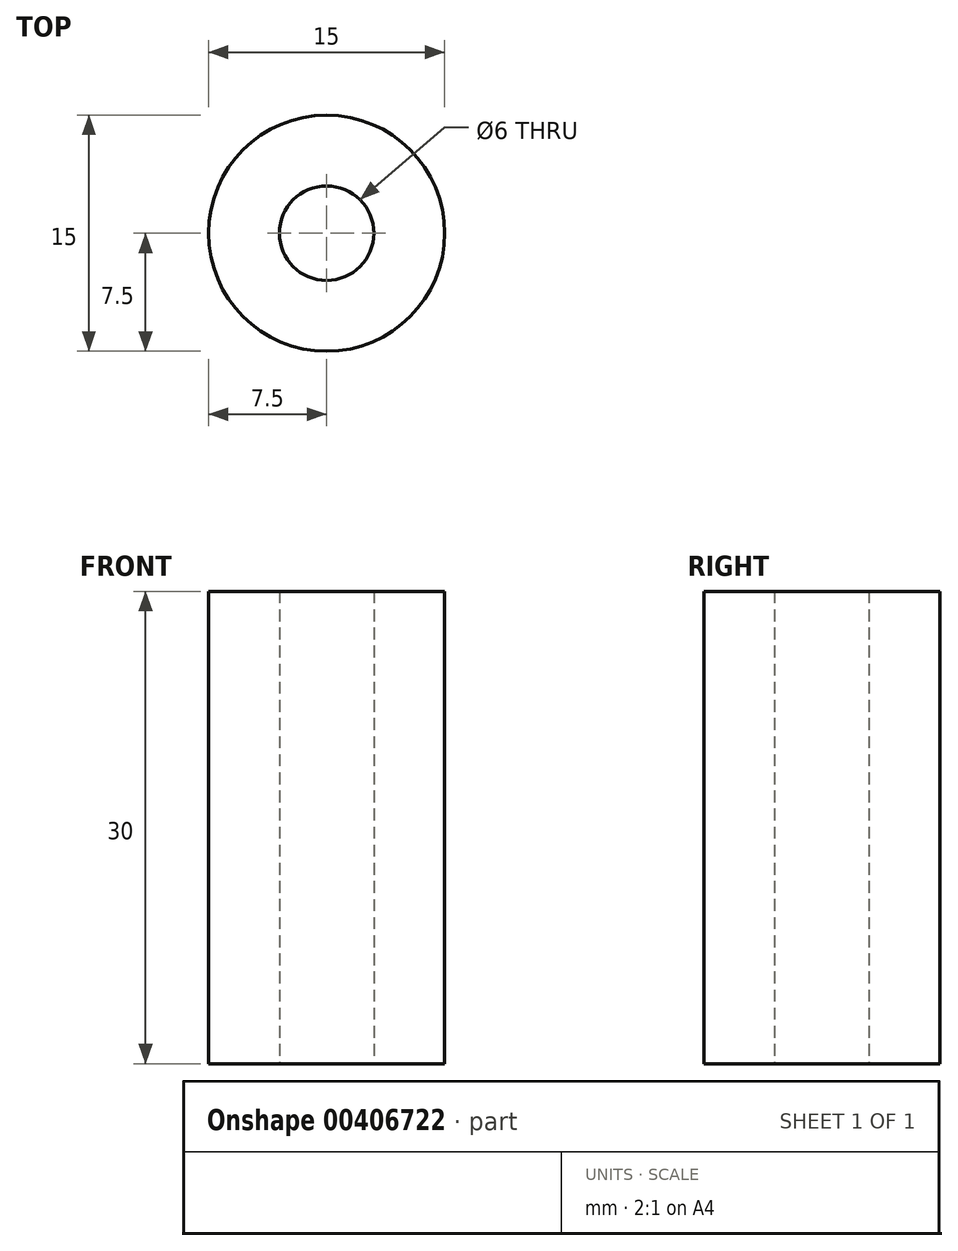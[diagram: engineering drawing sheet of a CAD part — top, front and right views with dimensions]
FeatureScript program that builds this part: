
annotation { "Feature Type Name" : "Feature", "Feature Type Description" : "" }
export const myFeature = defineFeature(function(context is Context, id is Id, definition is map)
    precondition{}
    {
        {
            var Q0;
            Q0=qCreatedBy(makeId("Top.planeOp"),FACE);
            var sketch = newSketch(context, id + "F0", { "sketchPlane" : qUnion([Q0])});
            skCircle(sketch, "E0", {"center": v(0, 0) * mm, "radius": 3 * mm});
            skCircle(sketch, "E1", {"center": v(0, 0) * mm, "radius": 7.5 * mm});
            skSolve(sketch);
        }
        {
            var Q0;
            Q0=makeQuery(id+"F0.imprint","IMPRINT",FACE,{"disambiguationData":[TD([[makeQuery(id+"F0.imprint","IMPRINT",EDGE,{"derivedFrom":sQuery(id+"F0.wireOp",EDGE,"E0")}),-1.0]])]});
            extrude(context, id + "F1", {"entities" : qUnion([Q0]), "depth" : 30 * mm});
        }
    });
